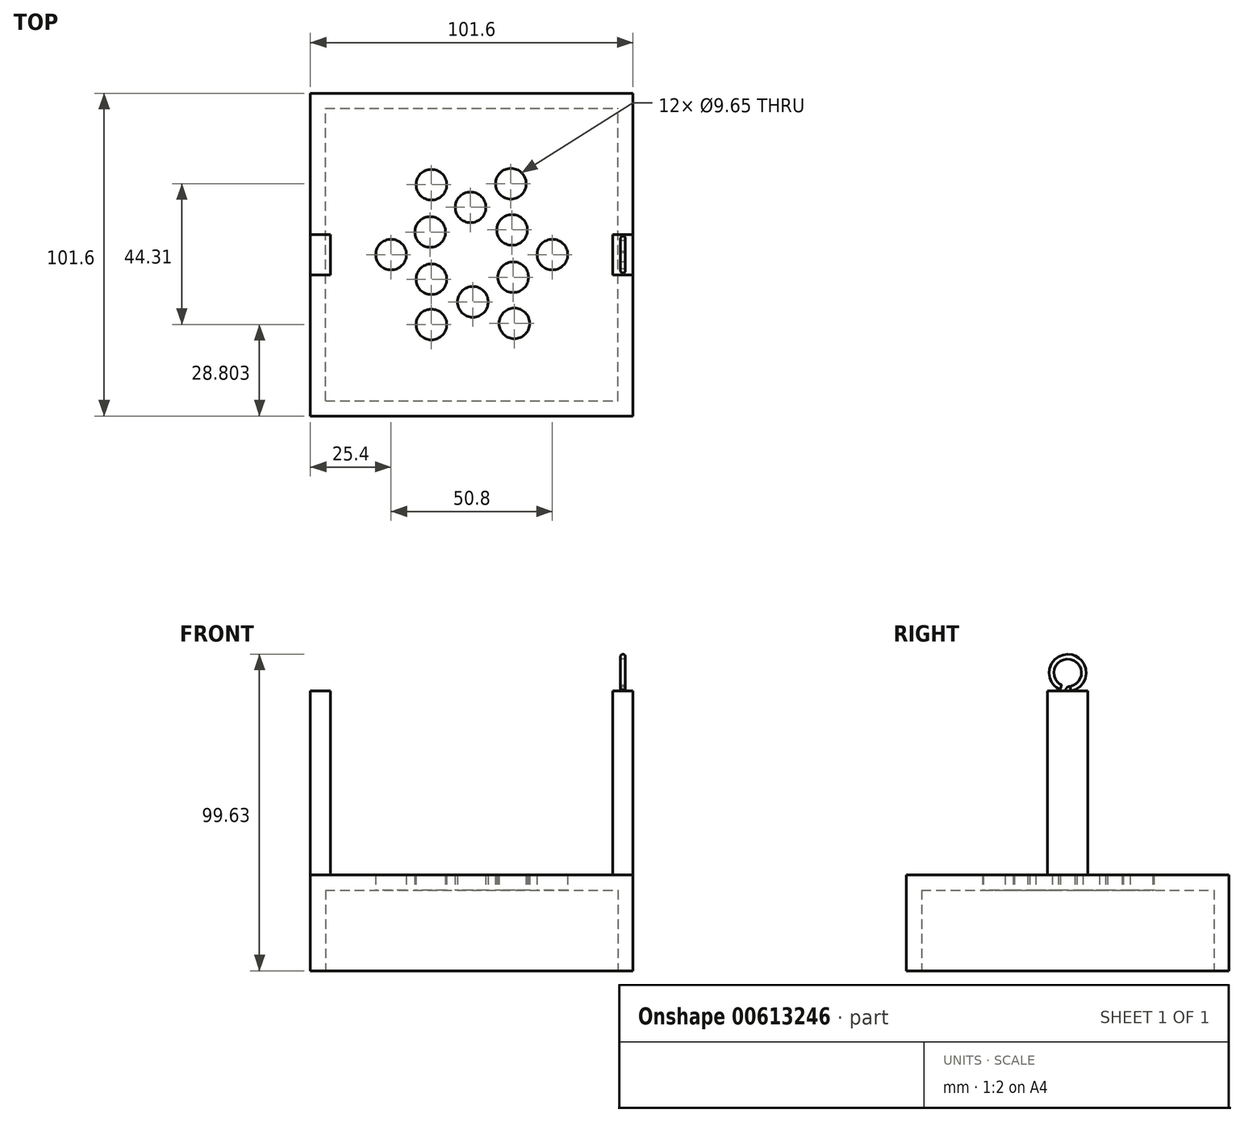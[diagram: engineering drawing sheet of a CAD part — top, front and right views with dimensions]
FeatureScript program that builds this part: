
annotation { "Feature Type Name" : "Feature", "Feature Type Description" : "" }
export const myFeature = defineFeature(function(context is Context, id is Id, definition is map)
    precondition{}
    {
        {
            var Q0;
            Q0=qCreatedBy(makeId("Top.planeOp"),FACE);
            var sketch = newSketch(context, id + "F0", { "sketchPlane" : qUnion([Q0])});
            skLineSegment(sketch, "E0.bottom", {"start": v(0, 0) * mm, "end": v(101.6, 0) * mm});
            skLineSegment(sketch, "E0.top", {"start": v(0, 101.6) * mm, "end": v(101.6, 101.6) * mm});
            skLineSegment(sketch, "E0.left", {"start": v(0, 0) * mm, "end": v(0, 101.6) * mm});
            skLineSegment(sketch, "E0.right", {"start": v(101.6, 0) * mm, "end": v(101.6, 101.6) * mm});
            skPoint(sketch, "E1.cCircle.centerSnap0", {"position": v(101.6, 50.8) * mm});
            skPoint(sketch, "E1.cCircle.centerSnap1", {"position": v(50.8, 101.6) * mm});
            skPoint(sketch, "E1.cCircle.perimeterSnap0", {"position": v(101.6, 50.8) * mm});
            skPoint(sketch, "E1.0.startSnap0", {"position": v(101.6, 50.8) * mm});
            skCircle(sketch, "E2", {"center": v(38.1, 72.8) * mm, "radius": 4.83 * mm});
            skCircle(sketch, "E3", {"center": v(63.14, 73.11) * mm, "radius": 4.83 * mm});
            skCircle(sketch, "E4", {"center": v(76.2, 50.8) * mm, "radius": 4.83 * mm});
            skCircle(sketch, "E5", {"center": v(64.24, 29.13) * mm, "radius": 4.83 * mm});
            skCircle(sketch, "E6", {"center": v(38.1, 28.8) * mm, "radius": 4.83 * mm});
            skCircle(sketch, "E7", {"center": v(25.4, 50.8) * mm, "radius": 4.83 * mm});
            skCircle(sketch, "E8", {"center": v(50.43, 65.68) * mm, "radius": 4.83 * mm});
            skCircle(sketch, "E9", {"center": v(63.5, 58.56) * mm, "radius": 4.83 * mm});
            skCircle(sketch, "E10", {"center": v(63.87, 43.68) * mm, "radius": 4.83 * mm});
            skCircle(sketch, "E11", {"center": v(51.17, 35.92) * mm, "radius": 4.83 * mm});
            skCircle(sketch, "E12", {"center": v(38.1, 43.04) * mm, "radius": 4.83 * mm});
            skCircle(sketch, "E13", {"center": v(37.73, 57.92) * mm, "radius": 4.83 * mm});
            skSolve(sketch);
        }
        {
            var Q0;
            Q0=makeQuery(id+"F0.imprint","IMPRINT",FACE,{"disambiguationData":[TD([[makeQuery(id+"F0.imprint","IMPRINT",EDGE,{"derivedFrom":sQuery(id+"F0.wireOp",EDGE,"E0.bottom")}),1.0]])]});
            var Q1;
            Q1=makeQuery(id+"F0.imprint","IMPRINT",FACE,{"disambiguationData":[TD([[makeQuery(id+"F0.imprint","IMPRINT",EDGE,{"derivedFrom":sQuery(id+"F0.wireOp",EDGE,"E9")}),1.0]])]});
            var Q2;
            Q2=makeQuery(id+"F0.imprint","IMPRINT",FACE,{"disambiguationData":[TD([[makeQuery(id+"F0.imprint","IMPRINT",EDGE,{"derivedFrom":sQuery(id+"F0.wireOp",EDGE,"E3")}),1.0]])]});
            var Q3;
            Q3=makeQuery(id+"F0.imprint","IMPRINT",FACE,{"disambiguationData":[TD([[makeQuery(id+"F0.imprint","IMPRINT",EDGE,{"derivedFrom":sQuery(id+"F0.wireOp",EDGE,"E8")}),1.0]])]});
            var Q4;
            Q4=makeQuery(id+"F0.imprint","IMPRINT",FACE,{"disambiguationData":[TD([[makeQuery(id+"F0.imprint","IMPRINT",EDGE,{"derivedFrom":sQuery(id+"F0.wireOp",EDGE,"E2")}),1.0]])]});
            var Q5;
            Q5=makeQuery(id+"F0.imprint","IMPRINT",FACE,{"disambiguationData":[TD([[makeQuery(id+"F0.imprint","IMPRINT",EDGE,{"derivedFrom":sQuery(id+"F0.wireOp",EDGE,"E13")}),1.0]])]});
            var Q6;
            Q6=makeQuery(id+"F0.imprint","IMPRINT",FACE,{"disambiguationData":[TD([[makeQuery(id+"F0.imprint","IMPRINT",EDGE,{"derivedFrom":sQuery(id+"F0.wireOp",EDGE,"E7")}),1.0]])]});
            var Q7;
            Q7=makeQuery(id+"F0.imprint","IMPRINT",FACE,{"disambiguationData":[TD([[makeQuery(id+"F0.imprint","IMPRINT",EDGE,{"derivedFrom":sQuery(id+"F0.wireOp",EDGE,"E12")}),1.0]])]});
            var Q8;
            Q8=makeQuery(id+"F0.imprint","IMPRINT",FACE,{"disambiguationData":[TD([[makeQuery(id+"F0.imprint","IMPRINT",EDGE,{"derivedFrom":sQuery(id+"F0.wireOp",EDGE,"E6")}),1.0]])]});
            var Q9;
            Q9=makeQuery(id+"F0.imprint","IMPRINT",FACE,{"disambiguationData":[TD([[makeQuery(id+"F0.imprint","IMPRINT",EDGE,{"derivedFrom":sQuery(id+"F0.wireOp",EDGE,"E11")}),1.0]])]});
            var Q10;
            Q10=makeQuery(id+"F0.imprint","IMPRINT",FACE,{"disambiguationData":[TD([[makeQuery(id+"F0.imprint","IMPRINT",EDGE,{"derivedFrom":sQuery(id+"F0.wireOp",EDGE,"E10")}),1.0]])]});
            var Q11;
            Q11=makeQuery(id+"F0.imprint","IMPRINT",FACE,{"disambiguationData":[TD([[makeQuery(id+"F0.imprint","IMPRINT",EDGE,{"derivedFrom":sQuery(id+"F0.wireOp",EDGE,"E4")}),1.0]])]});
            var Q12;
            Q12=makeQuery(id+"F0.imprint","IMPRINT",FACE,{"disambiguationData":[TD([[makeQuery(id+"F0.imprint","IMPRINT",EDGE,{"derivedFrom":sQuery(id+"F0.wireOp",EDGE,"E5")}),1.0]])]});
            extrude(context, id + "F1", {"entities" : qUnion([Q0, Q1, Q2, Q3, Q4, Q5, Q6, Q7, Q8, Q9, Q10, Q11, Q12]), "depth" : 30.16 * mm, "offsetDistance" : 25.4 * mm});
        }
        {
            var Q0;
            Q0=makeQuery(id+"F1.opExtrude","CAP_FACE",FACE,{"disambiguationData":[OSD([sQuery(id+"F0.wireOp",EDGE,"E0.bottom"),sQuery(id+"F0.wireOp",EDGE,"E0.top"),sQuery(id+"F0.wireOp",EDGE,"E0.left"),sQuery(id+"F0.wireOp",EDGE,"E0.right")])],"isStart":true});
            shell(context, id + "F2", {"entities" : qUnion([Q0]), "thickness" : 4.76 * mm});
        }
        {
            var Q0;
            Q0=makeQuery(id+"F0.imprint","IMPRINT",FACE,{"disambiguationData":[TD([[makeQuery(id+"F0.imprint","IMPRINT",EDGE,{"derivedFrom":sQuery(id+"F0.wireOp",EDGE,"E4")}),1.0]])]});
            var Q1;
            Q1=makeQuery(id+"F0.imprint","IMPRINT",FACE,{"disambiguationData":[TD([[makeQuery(id+"F0.imprint","IMPRINT",EDGE,{"derivedFrom":sQuery(id+"F0.wireOp",EDGE,"E9")}),1.0]])]});
            var Q2;
            Q2=makeQuery(id+"F0.imprint","IMPRINT",FACE,{"disambiguationData":[TD([[makeQuery(id+"F0.imprint","IMPRINT",EDGE,{"derivedFrom":sQuery(id+"F0.wireOp",EDGE,"E3")}),1.0]])]});
            var Q3;
            Q3=makeQuery(id+"F0.imprint","IMPRINT",FACE,{"disambiguationData":[TD([[makeQuery(id+"F0.imprint","IMPRINT",EDGE,{"derivedFrom":sQuery(id+"F0.wireOp",EDGE,"E8")}),1.0]])]});
            var Q4;
            Q4=makeQuery(id+"F0.imprint","IMPRINT",FACE,{"disambiguationData":[TD([[makeQuery(id+"F0.imprint","IMPRINT",EDGE,{"derivedFrom":sQuery(id+"F0.wireOp",EDGE,"E2")}),1.0]])]});
            var Q5;
            Q5=makeQuery(id+"F0.imprint","IMPRINT",FACE,{"disambiguationData":[TD([[makeQuery(id+"F0.imprint","IMPRINT",EDGE,{"derivedFrom":sQuery(id+"F0.wireOp",EDGE,"E13")}),1.0]])]});
            var Q6;
            Q6=makeQuery(id+"F0.imprint","IMPRINT",FACE,{"disambiguationData":[TD([[makeQuery(id+"F0.imprint","IMPRINT",EDGE,{"derivedFrom":sQuery(id+"F0.wireOp",EDGE,"E7")}),1.0]])]});
            var Q7;
            Q7=makeQuery(id+"F0.imprint","IMPRINT",FACE,{"disambiguationData":[TD([[makeQuery(id+"F0.imprint","IMPRINT",EDGE,{"derivedFrom":sQuery(id+"F0.wireOp",EDGE,"E12")}),1.0]])]});
            var Q8;
            Q8=makeQuery(id+"F0.imprint","IMPRINT",FACE,{"disambiguationData":[TD([[makeQuery(id+"F0.imprint","IMPRINT",EDGE,{"derivedFrom":sQuery(id+"F0.wireOp",EDGE,"E10")}),1.0]])]});
            var Q9;
            Q9=makeQuery(id+"F0.imprint","IMPRINT",FACE,{"disambiguationData":[TD([[makeQuery(id+"F0.imprint","IMPRINT",EDGE,{"derivedFrom":sQuery(id+"F0.wireOp",EDGE,"E5")}),1.0]])]});
            var Q10;
            Q10=makeQuery(id+"F0.imprint","IMPRINT",FACE,{"disambiguationData":[TD([[makeQuery(id+"F0.imprint","IMPRINT",EDGE,{"derivedFrom":sQuery(id+"F0.wireOp",EDGE,"E11")}),1.0]])]});
            var Q11;
            Q11=makeQuery(id+"F0.imprint","IMPRINT",FACE,{"disambiguationData":[TD([[makeQuery(id+"F0.imprint","IMPRINT",EDGE,{"derivedFrom":sQuery(id+"F0.wireOp",EDGE,"E6")}),1.0]])]});
            extrude(context, id + "F3", {"entities" : qUnion([Q0, Q1, Q2, Q3, Q4, Q5, Q6, Q7, Q8, Q9, Q10, Q11]), "operationType" : NewBodyOperationType.REMOVE, "depth" : 49.02 * mm, "offsetDistance" : 25.4 * mm});
        }
        {
            var Q0;
            Q0=makeQuery(id+"F1.opExtrude","CAP_FACE",FACE,{"disambiguationData":[OSD([sQuery(id+"F0.wireOp",EDGE,"E0.bottom"),sQuery(id+"F0.wireOp",EDGE,"E0.top"),sQuery(id+"F0.wireOp",EDGE,"E0.left"),sQuery(id+"F0.wireOp",EDGE,"E0.right")])],"isStart":false});
            cPlane(context, id + "F4", {"entities" : qUnion([Q0]), "cplaneType" : CPlaneType.OFFSET, "offset" : 0 * mm, "width" : 152.4 * mm, "height" : 152.4 * mm});
        }
        {
            var Q0;
            Q0=qCreatedBy(id+"F4.planeOp",FACE);
            var sketch = newSketch(context, id + "F5", { "sketchPlane" : qUnion([Q0])});
            skLineSegment(sketch, "E14.bottom", {"start": v(0, 0) * mm, "end": v(0, 0) * mm});
            skLineSegment(sketch, "E14.top", {"start": v(0, 101.6) * mm, "end": v(0, 101.6) * mm});
            skLineSegment(sketch, "E15.left", {"start": v(0, 57.15) * mm, "end": v(0, 50.8) * mm});
            skLineSegment(sketch, "E15.right", {"start": v(6.35, 57.15) * mm, "end": v(6.35, 50.8) * mm});
            skLineSegment(sketch, "E16.bottom", {"start": v(0, 57.15) * mm, "end": v(6.35, 57.15) * mm});
            skPoint(sketch, "E17.orphan", {"position": v(6.35, 101.6) * mm});
            skPoint(sketch, "E15.top.end.orphan", {"position": v(6.35, 0) * mm});
            skPoint(sketch, "E15.top.start.orphan", {"position": v(0, 0) * mm});
            skLineSegment(sketch, "E18.MirrorCS", {"start": v(0, 44.45) * mm, "end": v(6.35, 44.45) * mm});
            skLineSegment(sketch, "E19.MirrorCS", {"start": v(6.35, 44.45) * mm, "end": v(6.35, 50.8) * mm});
            skLineSegment(sketch, "E20.MirrorCS", {"start": v(0, 44.45) * mm, "end": v(0, 50.8) * mm});
            skLineSegment(sketch, "E21.left", {"start": v(0, 57.15) * mm, "end": v(0, 44.45) * mm});
            skLineSegment(sketch, "E21.right", {"start": v(101.6, 57.15) * mm, "end": v(101.6, 44.45) * mm});
            skLineSegment(sketch, "E22.MirrorCS", {"start": v(101.6, 57.15) * mm, "end": v(95.25, 57.15) * mm});
            skLineSegment(sketch, "E23.MirrorCS", {"start": v(95.25, 57.15) * mm, "end": v(95.25, 50.8) * mm});
            skLineSegment(sketch, "E24.MirrorCS", {"start": v(95.25, 44.45) * mm, "end": v(95.25, 50.8) * mm});
            skLineSegment(sketch, "E25.MirrorCS", {"start": v(101.6, 44.45) * mm, "end": v(95.25, 44.45) * mm});
            skPoint(sketch, "E26.start.orphan", {"position": v(50.8, 101.6) * mm});
            skPoint(sketch, "E27.trimOffspring.start.orphan", {"position": v(50.8, 0) * mm});
            skPoint(sketch, "E28.orphan", {"position": v(101.6, 0) * mm});
            skPoint(sketch, "E29.orphan", {"position": v(101.6, 101.6) * mm});
            skSolve(sketch);
        }
        {
            var Q0;
            Q0 = qSketchRegion(id + "F5", true);
            extrude(context, id + "F6", {"entities" : qUnion([Q0]), "depth" : 57.9 * mm, "offsetDistance" : 25.4 * mm});
        }
        {
            var Q0;
            Q0=makeQuery(id+"F6.opExtrude","SWEPT_FACE",FACE,{"disambiguationData":[OSD([sQuery(id+"F5.wireOp",EDGE,"E21.right")])]});
            cPlane(context, id + "F7", {"entities" : qUnion([Q0]), "cplaneType" : CPlaneType.OFFSET, "offset" : 3.17 * mm, "oppositeDirection" : true, "width" : 152.4 * mm, "height" : 152.4 * mm});
        }
        {
            var Q0;
            Q0=qCreatedBy(id+"F7.planeOp",FACE);
            var sketch = newSketch(context, id + "F8", { "sketchPlane" : qUnion([Q0])});
            skLineSegment(sketch, "E30.right", {"start": v(55.88, 75.06) * mm, "end": v(55.88, 88.72) * mm});
            skLineSegment(sketch, "E31", {"start": v(45.72, 88.72) * mm, "end": v(45.72, 88.72) * mm});
            skLineSegment(sketch, "E32", {"start": v(55.88, 88.72) * mm, "end": v(55.88, 88.72) * mm});
            skPoint(sketch, "E33.centerSnap0", {"position": v(50.8, 98.88) * mm});
            skPoint(sketch, "E34.centerSnap0", {"position": v(55.88, 93.8) * mm});
            skPoint(sketch, "E35", {"position": v(45.72, 93.8) * mm});
            skLineSegment(sketch, "E36", {"start": v(45.72, 93.8) * mm, "end": v(45.72, 93.8) * mm});
            skPoint(sketch, "E37", {"position": v(50.8, 75.06) * mm});
            skArc(sketch, "E38", {"start": v(51.64, 88.79) * mm, "mid": v(51.49, 98.83) * mm, "end": v(48.64, 89.2) * mm});
            skLineSegment(sketch, "E39", {"start": v(50.8, 88.06) * mm, "end": v(50.8, 87.53) * mm});
            skPoint(sketch, "E40", {"position": v(48.64, 89.2) * mm});
            skPoint(sketch, "E41.orphan", {"position": v(50.8, 88.72) * mm});
            skPoint(sketch, "E42", {"position": v(50.8, 87.53) * mm});
            skArc(sketch, "E43", {"start": v(51.64, 88.79) * mm, "mid": v(51.09, 88.58) * mm, "end": v(50.8, 88.06) * mm});
            skPoint(sketch, "E44.orphan", {"position": v(50.8, 88.1) * mm});
            skPoint(sketch, "E45.orphan", {"position": v(50.8, 87.82) * mm});
            skSolve(sketch);
        }
        {
            var Q0;
            Q0=makeQuery(id+"F6.opExtrude","CAP_FACE",FACE,{"disambiguationData":[OSD([sQuery(id+"F5.wireOp",EDGE,"E22.MirrorCS"),sQuery(id+"F5.wireOp",EDGE,"E23.MirrorCS"),sQuery(id+"F5.wireOp",EDGE,"E24.MirrorCS"),sQuery(id+"F5.wireOp",EDGE,"E25.MirrorCS"),sQuery(id+"F5.wireOp",EDGE,"E21.right")])],"isStart":false});
            var sketch = newSketch(context, id + "F9", { "sketchPlane" : qUnion([Q0])});
            skPoint(sketch, "E46.0", {"position": v(98.43, 50.8) * mm});
            skCircle(sketch, "E47", {"center": v(98.43, 50.8) * mm, "radius": 0.76 * mm});
            skSolve(sketch);
        }
        {
            var Q0;
            Q0=makeQuery(id+"F9.imprint","IMPRINT",FACE,{"disambiguationData":[TD([[makeQuery(id+"F9.imprint","IMPRINT",EDGE,{"derivedFrom":sQuery(id+"F9.wireOp",EDGE,"E47")}),1.0]])]});
            var Q1;
            Q1=sQuery(id+"F8.wireOp",EDGE,"E38");
            var Q2;
            Q2=sQuery(id+"F8.wireOp",EDGE,"E43");
            sweep(context, id + "F10", {"profiles" : qUnion([Q0]), "path" : qUnion([Q1, Q2])});
        }
    });
